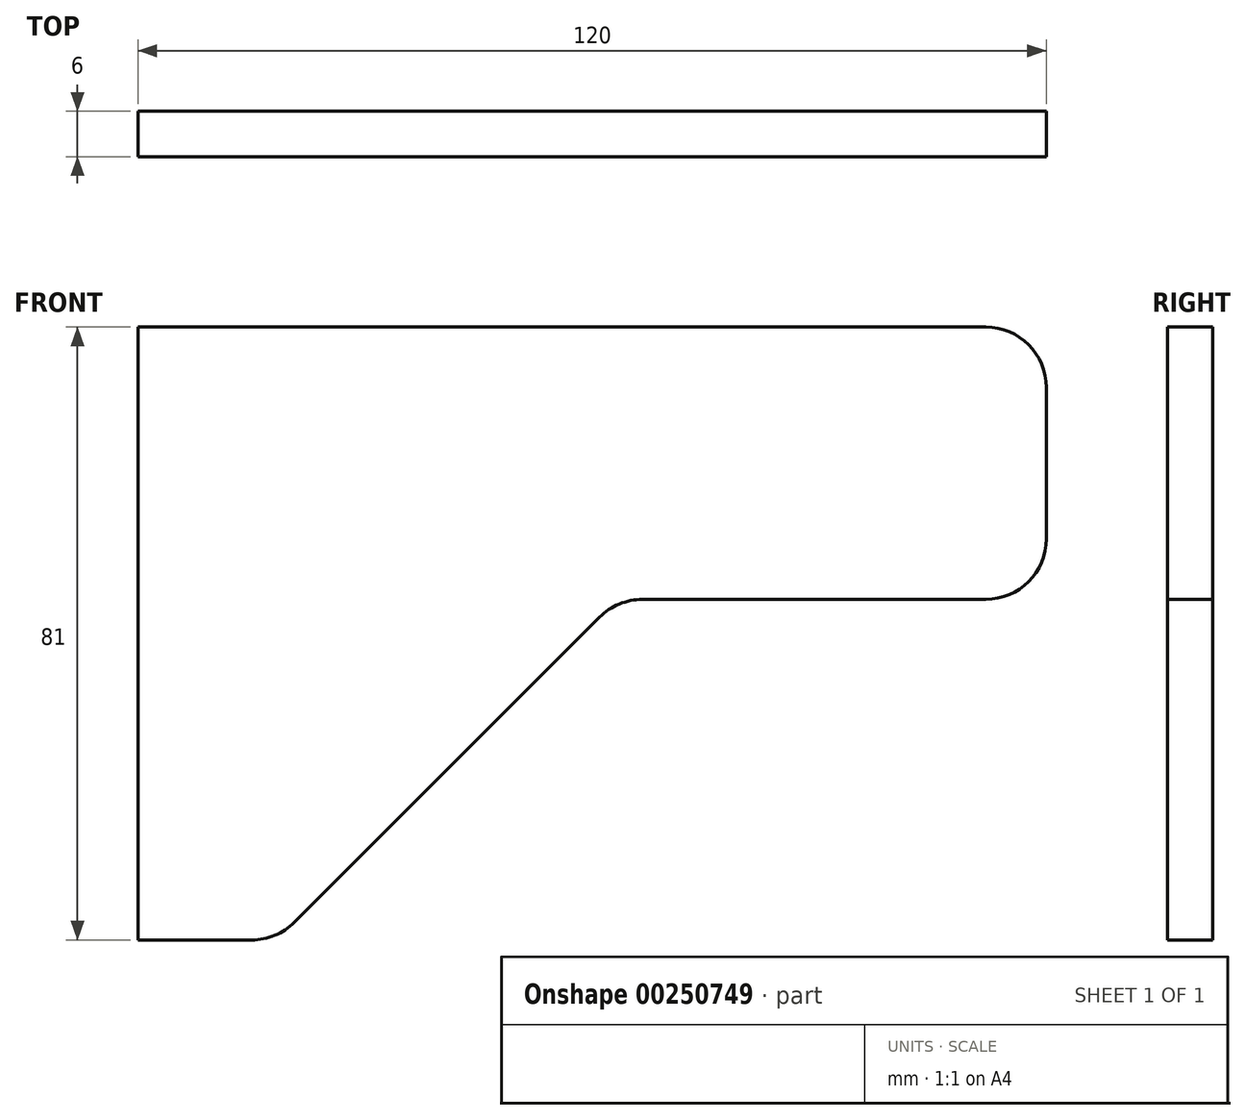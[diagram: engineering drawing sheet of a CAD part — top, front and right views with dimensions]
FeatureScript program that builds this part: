
annotation { "Feature Type Name" : "Feature", "Feature Type Description" : "" }
export const myFeature = defineFeature(function(context is Context, id is Id, definition is map)
    precondition{}
    {
        {
            var Q0;
            Q0=qCreatedBy(makeId("Front.planeOp"),FACE);
            var sketch = newSketch(context, id + "F0", { "sketchPlane" : qUnion([Q0])});
            skLineSegment(sketch, "E0", {"start": v(20.66, -78.66) * mm, "end": v(60.97, -38.34) * mm});
            skLineSegment(sketch, "E1.bottom", {"start": v(-6, 0) * mm, "end": v(0, 0) * mm, "construction": true});
            skLineSegment(sketch, "E1.top", {"start": v(-6, -81) * mm, "end": v(0, -81) * mm, "construction": true});
            skLineSegment(sketch, "E1.left", {"start": v(-6, 0) * mm, "end": v(-6, -81) * mm, "construction": true});
            skLineSegment(sketch, "E1.right", {"start": v(0, 0) * mm, "end": v(0, -81) * mm});
            skLineSegment(sketch, "E2", {"start": v(120, -8) * mm, "end": v(120, -28) * mm});
            skLineSegment(sketch, "E3", {"start": v(112, -36) * mm, "end": v(66.63, -36) * mm});
            skLineSegment(sketch, "E4", {"start": v(112, 0) * mm, "end": v(0, 0) * mm});
            skLineSegment(sketch, "E5", {"start": v(0, -81) * mm, "end": v(15, -81) * mm});
            skArc(sketch, "E6.filletArc", {"start": v(120, -8) * mm, "mid": v(117.66, -2.34) * mm, "end": v(112, 0) * mm});
            skArc(sketch, "E7.filletArc", {"start": v(112, -36) * mm, "mid": v(117.66, -33.66) * mm, "end": v(120, -28) * mm});
            skArc(sketch, "E8.filletArc", {"start": v(66.63, -36) * mm, "mid": v(63.57, -36.6) * mm, "end": v(60.97, -38.34) * mm});
            skArc(sketch, "E9.filletArc", {"start": v(15, -81) * mm, "mid": v(18.06, -80.4) * mm, "end": v(20.66, -78.66) * mm});
            skLineSegment(sketch, "E10", {"start": v(114.63, -21) * mm, "end": v(56.63, -21) * mm, "construction": true});
            skLineSegment(sketch, "E11", {"start": v(56.63, -21) * mm, "end": v(34, -43.63) * mm, "construction": true});
            skLineSegment(sketch, "E12", {"start": v(34, -43.63) * mm, "end": v(0, -43.63) * mm, "construction": true});
            skSolve(sketch);
        }
        {
            var Q0;
            Q0 = qSketchRegion(id + "F0", true);
            extrude(context, id + "F1", {"entities" : qUnion([Q0]), "depth" : 6 * mm});
        }
    });
